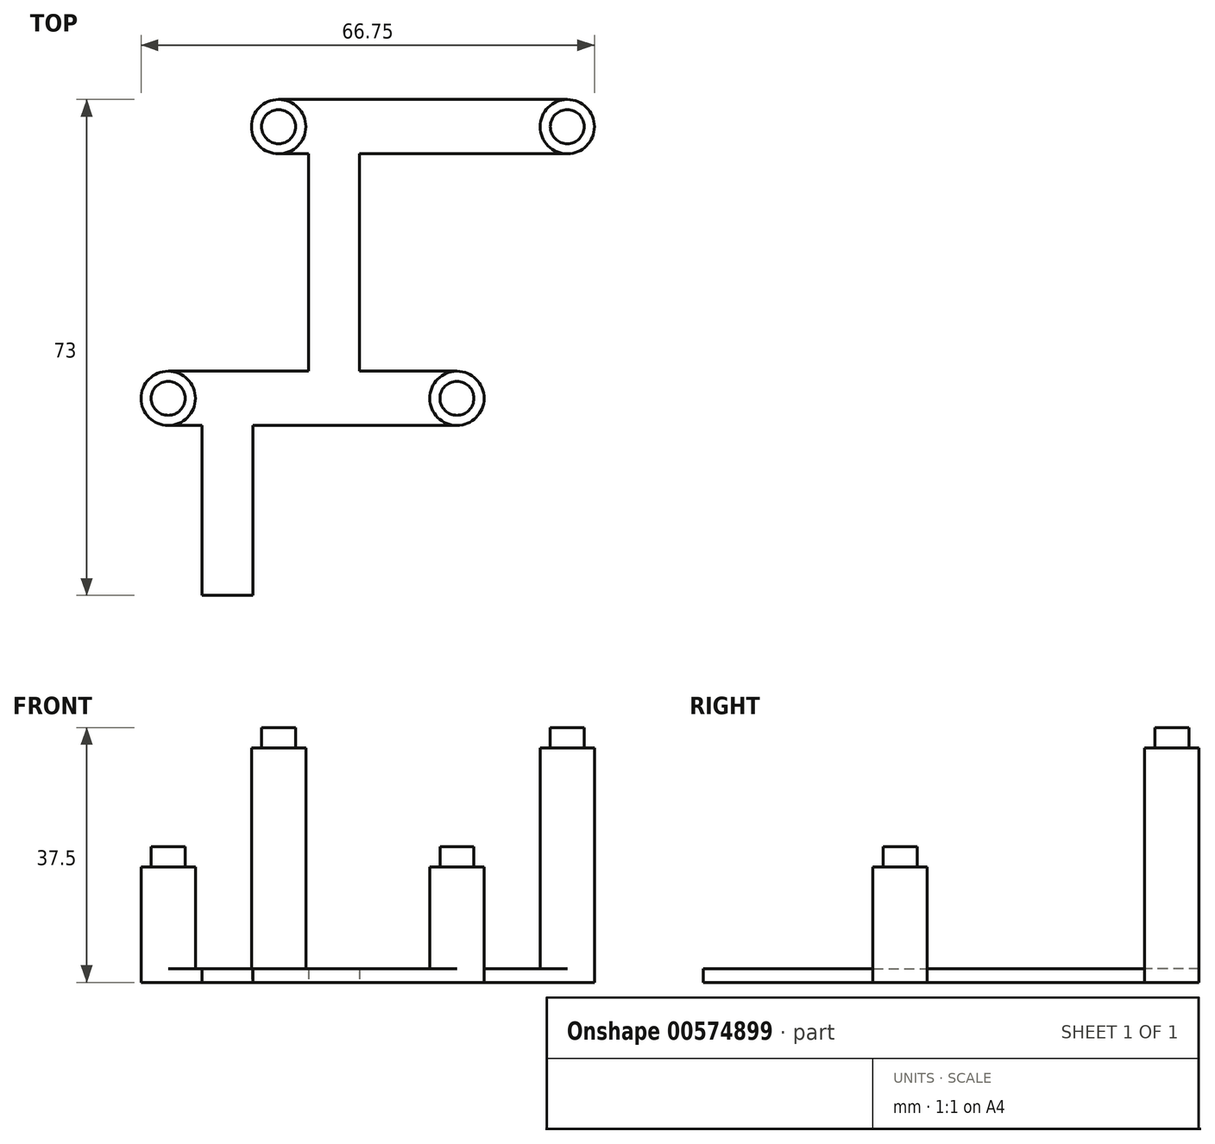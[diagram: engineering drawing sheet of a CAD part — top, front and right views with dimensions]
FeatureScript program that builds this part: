
annotation { "Feature Type Name" : "Feature", "Feature Type Description" : "" }
export const myFeature = defineFeature(function(context is Context, id is Id, definition is map)
    precondition{}
    {
        {
            assignVariable(context, id + "F0", {"name" : "ID", "anyValue" : 30});
        }
        {
            assignVariable(context, id + "F1", {"name" : "OD", "anyValue" : 32.5});
        }
        {
            assignVariable(context, id + "F2", {"name" : "HShift", "anyValue" : getVariable(context, 'OD') / 2});
        }
        {
            assignVariable(context, id + "F3", {"name" : "VShift", "anyValue" : getVariable(context, 'ID') / 2});
        }
        {
            assignVariable(context, id + "F4", {"name" : "Base", "anyValue" : 2});
        }
        {
            var Q0;
            Q0=qCreatedBy(makeId("Top.planeOp"),FACE);
            var sketch = newSketch(context, id + "F5", { "sketchPlane" : qUnion([Q0])});
            skCircle(sketch, "E0", {"center": v(0, 0) * mm, "radius": 4 * mm});
            skCircle(sketch, "E1", {"center": v(0, 0) * mm, "radius": 2.5 * mm});
            skCircle(sketch, "E2.0.1.0", {"center": v(0, -40) * mm, "radius": 4 * mm});
            skCircle(sketch, "E2.0.1.1", {"center": v(0, -40) * mm, "radius": 2.5 * mm});
            skCircle(sketch, "E2.1.0.0", {"center": v(42.5, 0) * mm, "radius": 4 * mm});
            skCircle(sketch, "E2.1.0.1", {"center": v(42.5, 0) * mm, "radius": 2.5 * mm});
            skCircle(sketch, "E2.1.1.0", {"center": v(42.5, -40) * mm, "radius": 4 * mm});
            skCircle(sketch, "E2.1.1.1", {"center": v(42.5, -40) * mm, "radius": 2.5 * mm});
            skLineSegment(sketch, "E2.direction1", {"start": v(0, 0) * mm, "end": v(42.5, 0) * mm, "construction": true});
            skLineSegment(sketch, "E2.direction2", {"start": v(0, 0) * mm, "end": v(0, -40) * mm, "construction": true});
            skLineSegment(sketch, "E3", {"start": v(0, 4) * mm, "end": v(42.5, 4) * mm});
            skLineSegment(sketch, "E4.MirrorCS", {"start": v(0, -4) * mm, "end": v(42.5, -4) * mm});
            skLineSegment(sketch, "E5.0.1.0", {"start": v(0, -36) * mm, "end": v(42.5, -36) * mm});
            skLineSegment(sketch, "E5.0.1.1", {"start": v(0, -44) * mm, "end": v(42.5, -44) * mm});
            skLineSegment(sketch, "E5.direction1", {"start": v(0, -4) * mm, "end": v(20.5, -4) * mm, "construction": true});
            skLineSegment(sketch, "E5.direction2", {"start": v(0, -4) * mm, "end": v(0, -44) * mm, "construction": true});
            skSolve(sketch);
        }
        {
            var Q0;
            {var subQ0=sQuery(id+"F5.wireOp",EDGE,"E3");Q0=makeQuery(id+"F5.imprint","IMPRINT",FACE,{"disambiguationData":[TD([[makeQuery(id+"F5.imprint","IMPRINT",EDGE,{"derivedFrom":subQ0}),-1.0]])]});}
            var Q1;
            Q1=makeQuery(id+"F5.imprint","IMPRINT",FACE,{"disambiguationData":[TD([[makeQuery(id+"F5.imprint","IMPRINT",EDGE,{"derivedFrom":sQuery(id+"F5.wireOp",EDGE,"E1")}),1.0]])]});
            var Q2;
            Q2=makeQuery(id+"F5.imprint","IMPRINT",FACE,{"disambiguationData":[TD([[makeQuery(id+"F5.imprint","IMPRINT",EDGE,{"derivedFrom":sQuery(id+"F5.wireOp",EDGE,"E1")}),-1.0]])]});
            var Q3;
            Q3=makeQuery(id+"F5.imprint","IMPRINT",FACE,{"disambiguationData":[TD([[makeQuery(id+"F5.imprint","IMPRINT",EDGE,{"derivedFrom":sQuery(id+"F5.wireOp",EDGE,"E2.1.0.1")}),1.0]])]});
            var Q4;
            Q4=makeQuery(id+"F5.imprint","IMPRINT",FACE,{"disambiguationData":[TD([[makeQuery(id+"F5.imprint","IMPRINT",EDGE,{"derivedFrom":sQuery(id+"F5.wireOp",EDGE,"E2.1.0.1")}),-1.0]])]});
            var Q5;
            Q5=makeQuery(id+"F5.imprint","IMPRINT",FACE,{"disambiguationData":[TD([[makeQuery(id+"F5.imprint","IMPRINT",EDGE,{"derivedFrom":sQuery(id+"F5.wireOp",EDGE,"E2.0.1.1")}),1.0]])]});
            var Q6;
            Q6=makeQuery(id+"F5.imprint","IMPRINT",FACE,{"disambiguationData":[TD([[makeQuery(id+"F5.imprint","IMPRINT",EDGE,{"derivedFrom":sQuery(id+"F5.wireOp",EDGE,"E2.1.1.1")}),1.0]])]});
            var Q7;
            Q7=makeQuery(id+"F5.imprint","IMPRINT",FACE,{"disambiguationData":[TD([[makeQuery(id+"F5.imprint","IMPRINT",EDGE,{"derivedFrom":sQuery(id+"F5.wireOp",EDGE,"E2.1.1.1")}),-1.0]])]});
            var Q8;
            Q8=makeQuery(id+"F5.imprint","IMPRINT",FACE,{"disambiguationData":[TD([[makeQuery(id+"F5.imprint","IMPRINT",EDGE,{"derivedFrom":sQuery(id+"F5.wireOp",EDGE,"E2.0.1.1")}),-1.0]])]});
            var Q9;
            {var subQ0=sQuery(id+"F5.wireOp",EDGE,"E5.0.1.0");Q9=makeQuery(id+"F5.imprint","IMPRINT",FACE,{"disambiguationData":[TD([[makeQuery(id+"F5.imprint","IMPRINT",EDGE,{"derivedFrom":subQ0}),-1.0]])]});}
            extrude(context, id + "F6", {"entities" : qUnion([Q0, Q1, Q2, Q3, Q4, Q5, Q6, Q7, Q8, Q9]), "depth" : (getVariable(context, 'Base')) * mm, "offsetDistance" : 25 * mm});
        }
        {
            var Q0;
            Q0=makeQuery(id+"F5.imprint","IMPRINT",FACE,{"disambiguationData":[TD([[makeQuery(id+"F5.imprint","IMPRINT",EDGE,{"derivedFrom":sQuery(id+"F5.wireOp",EDGE,"E1")}),1.0]])]});
            var Q1;
            Q1=makeQuery(id+"F5.imprint","IMPRINT",FACE,{"disambiguationData":[TD([[makeQuery(id+"F5.imprint","IMPRINT",EDGE,{"derivedFrom":sQuery(id+"F5.wireOp",EDGE,"E2.1.0.1")}),1.0]])]});
            var Q2;
            Q2=makeQuery(id+"F5.imprint","IMPRINT",FACE,{"disambiguationData":[TD([[makeQuery(id+"F5.imprint","IMPRINT",EDGE,{"derivedFrom":sQuery(id+"F5.wireOp",EDGE,"E1")}),-1.0]])]});
            var Q3;
            Q3=makeQuery(id+"F5.imprint","IMPRINT",FACE,{"disambiguationData":[TD([[makeQuery(id+"F5.imprint","IMPRINT",EDGE,{"derivedFrom":sQuery(id+"F5.wireOp",EDGE,"E2.1.0.1")}),-1.0]])]});
            extrude(context, id + "F7", {"entities" : qUnion([Q0, Q1, Q2, Q3]), "operationType" : NewBodyOperationType.ADD, "depth" : (getVariable(context, 'OD') + getVariable(context, 'Base')) * mm, "offsetDistance" : 25 * mm});
        }
        {
            var Q0;
            Q0=makeQuery(id+"F5.imprint","IMPRINT",FACE,{"disambiguationData":[TD([[makeQuery(id+"F5.imprint","IMPRINT",EDGE,{"derivedFrom":sQuery(id+"F5.wireOp",EDGE,"E1")}),1.0]])]});
            var Q1;
            Q1=makeQuery(id+"F5.imprint","IMPRINT",FACE,{"disambiguationData":[TD([[makeQuery(id+"F5.imprint","IMPRINT",EDGE,{"derivedFrom":sQuery(id+"F5.wireOp",EDGE,"E2.1.0.1")}),1.0]])]});
            extrude(context, id + "F8", {"entities" : qUnion([Q0, Q1]), "operationType" : NewBodyOperationType.ADD, "depth" : (getVariable(context, 'OD') + getVariable(context, 'Base') + 3) * mm, "offsetDistance" : 25 * mm});
        }
        {
            var Q0;
            Q0=makeQuery(id+"F5.imprint","IMPRINT",FACE,{"disambiguationData":[TD([[makeQuery(id+"F5.imprint","IMPRINT",EDGE,{"derivedFrom":sQuery(id+"F5.wireOp",EDGE,"E2.0.1.1")}),-1.0]])]});
            var Q1;
            Q1=makeQuery(id+"F5.imprint","IMPRINT",FACE,{"disambiguationData":[TD([[makeQuery(id+"F5.imprint","IMPRINT",EDGE,{"derivedFrom":sQuery(id+"F5.wireOp",EDGE,"E2.1.1.1")}),-1.0]])]});
            var Q2;
            Q2=makeQuery(id+"F5.imprint","IMPRINT",FACE,{"disambiguationData":[TD([[makeQuery(id+"F5.imprint","IMPRINT",EDGE,{"derivedFrom":sQuery(id+"F5.wireOp",EDGE,"E2.0.1.1")}),1.0]])]});
            var Q3;
            Q3=makeQuery(id+"F5.imprint","IMPRINT",FACE,{"disambiguationData":[TD([[makeQuery(id+"F5.imprint","IMPRINT",EDGE,{"derivedFrom":sQuery(id+"F5.wireOp",EDGE,"E2.1.1.1")}),1.0]])]});
            extrude(context, id + "F9", {"entities" : qUnion([Q0, Q1, Q2, Q3]), "operationType" : NewBodyOperationType.ADD, "depth" : (getVariable(context, 'Base') + getVariable(context, 'VShift')) * mm, "offsetDistance" : 25 * mm});
        }
        {
            var Q0;
            Q0=makeQuery(id+"F5.imprint","IMPRINT",FACE,{"disambiguationData":[TD([[makeQuery(id+"F5.imprint","IMPRINT",EDGE,{"derivedFrom":sQuery(id+"F5.wireOp",EDGE,"E2.0.1.1")}),1.0]])]});
            var Q1;
            Q1=makeQuery(id+"F5.imprint","IMPRINT",FACE,{"disambiguationData":[TD([[makeQuery(id+"F5.imprint","IMPRINT",EDGE,{"derivedFrom":sQuery(id+"F5.wireOp",EDGE,"E2.1.1.1")}),1.0]])]});
            extrude(context, id + "F10", {"entities" : qUnion([Q0, Q1]), "operationType" : NewBodyOperationType.ADD, "depth" : (getVariable(context, 'Base') + getVariable(context, 'VShift') + 3) * mm, "offsetDistance" : 25 * mm});
        }
        {
            var Q0;
            Q0=makeQuery(id+"F6.opExtrude","SWEPT_BODY",BODY,{"disambiguationData":[OSD([sQuery(id+"F5.wireOp",EDGE,"E2.0.1.0"),sQuery(id+"F5.wireOp",EDGE,"E2.1.1.0"),sQuery(id+"F5.wireOp",EDGE,"E5.0.1.0"),sQuery(id+"F5.wireOp",EDGE,"E5.0.1.1")])]});
            transform(context, id + "F11", {"entities" : qUnion([Q0]), "transformType" : TransformType.TRANSLATION_3D, "dx" : -1 * (getVariable(context, 'HShift')) * mm, "dy" : 0 * mm, "dz" : 0 * mm, "makeCopy" : false});
        }
        {
            var Q0;
            Q0=qCreatedBy(makeId("Top.planeOp"),FACE);
            var sketch = newSketch(context, id + "F12", { "sketchPlane" : qUnion([Q0])});
            skLineSegment(sketch, "E6.bottom", {"start": v(4.42, -4) * mm, "end": v(11.92, -4) * mm});
            skLineSegment(sketch, "E6.top", {"start": v(4.42, -36) * mm, "end": v(11.92, -36) * mm});
            skLineSegment(sketch, "E6.left", {"start": v(4.42, -4) * mm, "end": v(4.42, -36) * mm});
            skLineSegment(sketch, "E6.right", {"start": v(11.92, -4) * mm, "end": v(11.92, -36) * mm});
            skLineSegment(sketch, "E7.bottom", {"start": v(-11.25, -44) * mm, "end": v(-3.75, -44) * mm});
            skLineSegment(sketch, "E7.top", {"start": v(-11.25, -69) * mm, "end": v(-3.75, -69) * mm});
            skLineSegment(sketch, "E7.left", {"start": v(-11.25, -44) * mm, "end": v(-11.25, -69) * mm});
            skLineSegment(sketch, "E7.right", {"start": v(-3.75, -44) * mm, "end": v(-3.75, -69) * mm});
            skLineSegment(sketch, "E8", {"start": v(-7.5, -44) * mm, "end": v(-7.5, -47.1) * mm, "construction": true});
            skSolve(sketch);
        }
        {
            var Q0;
            Q0=makeQuery(id+"F12.imprint","IMPRINT",FACE,{"disambiguationData":[TD([[makeQuery(id+"F12.imprint","IMPRINT",EDGE,{"derivedFrom":sQuery(id+"F12.wireOp",EDGE,"E6.bottom")}),-1.0]])]});
            var Q1;
            Q1=makeQuery(id+"F12.imprint","IMPRINT",FACE,{"disambiguationData":[TD([[makeQuery(id+"F12.imprint","IMPRINT",EDGE,{"derivedFrom":sQuery(id+"F12.wireOp",EDGE,"E7.bottom")}),-1.0]])]});
            extrude(context, id + "F13", {"entities" : qUnion([Q0, Q1]), "operationType" : NewBodyOperationType.ADD, "depth" : (getVariable(context, 'Base')) * mm, "offsetDistance" : 25 * mm});
        }
    });
